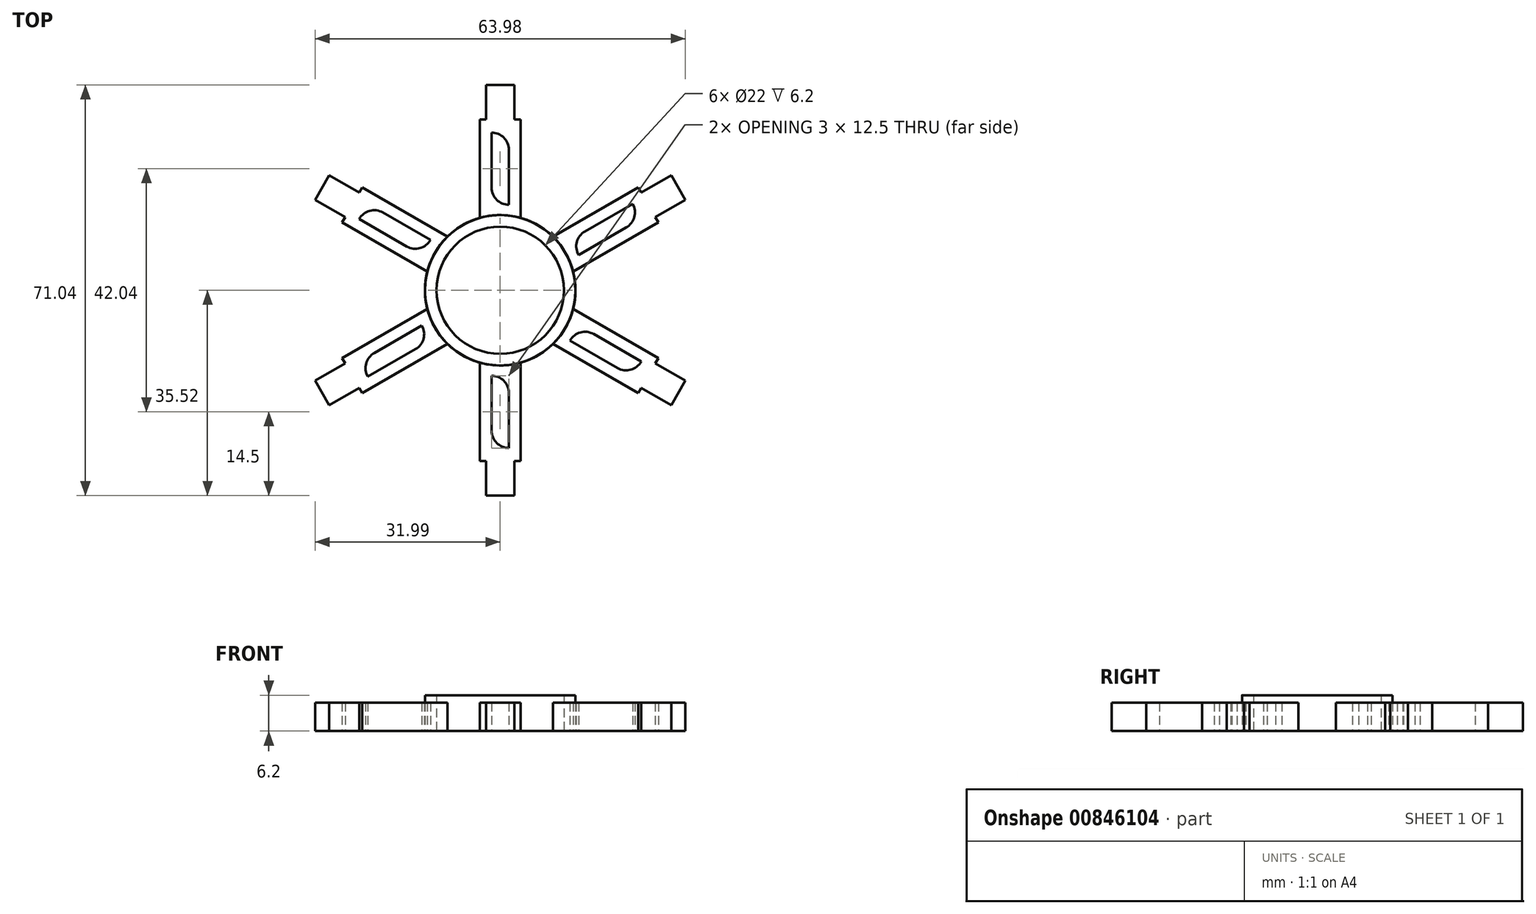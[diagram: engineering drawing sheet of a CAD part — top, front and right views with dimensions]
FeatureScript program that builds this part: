
annotation { "Feature Type Name" : "Feature", "Feature Type Description" : "" }
export const myFeature = defineFeature(function(context is Context, id is Id, definition is map)
    precondition{}
    {
        {
            var Q0;
            Q0=qCreatedBy(makeId("Top.planeOp"),FACE);
            var sketch = newSketch(context, id + "F0", { "sketchPlane" : qUnion([Q0])});
            skCircle(sketch, "E0", {"center": v(0, 0) * mm, "radius": 11 * mm});
            skLineSegment(sketch, "E1", {"start": v(0, 0) * mm, "end": v(11, 0) * mm});
            skCircle(sketch, "E2", {"center": v(0, 0) * mm, "radius": 13 * mm});
            skLineSegment(sketch, "E3", {"start": v(0, 0) * mm, "end": v(0, -13) * mm});
            skLineSegment(sketch, "E4.top", {"start": v(3.5, 29.52) * mm, "end": v(-3.5, 29.52) * mm});
            skLineSegment(sketch, "E4.left", {"start": v(3.5, 12.52) * mm, "end": v(3.5, 29.52) * mm});
            skLineSegment(sketch, "E4.right", {"start": v(-3.5, 12.52) * mm, "end": v(-3.5, 29.52) * mm});
            skPoint(sketch, "E4.middle", {"position": v(0, 21.02) * mm});
            skLineSegment(sketch, "E5.bottom", {"start": v(2.45, 29.52) * mm, "end": v(-2.45, 29.52) * mm});
            skLineSegment(sketch, "E5.top", {"start": v(2.45, 35.52) * mm, "end": v(-2.45, 35.52) * mm});
            skLineSegment(sketch, "E5.left", {"start": v(2.45, 29.52) * mm, "end": v(2.45, 35.52) * mm});
            skLineSegment(sketch, "E5.right", {"start": v(-2.45, 29.52) * mm, "end": v(-2.45, 35.52) * mm});
            skPoint(sketch, "E5.middle", {"position": v(0, 32.52) * mm});
            skLineSegment(sketch, "E6.bottom", {"start": v(1.5, 14.77) * mm, "end": v(1.5, 14.77) * mm});
            skLineSegment(sketch, "E6.top", {"start": v(-1.5, 27.27) * mm, "end": v(-1.5, 27.27) * mm});
            skLineSegment(sketch, "E6.left", {"start": v(1.5, 14.77) * mm, "end": v(1.5, 24.27) * mm});
            skLineSegment(sketch, "E6.right", {"start": v(-1.5, 17.77) * mm, "end": v(-1.5, 27.27) * mm});
            skPoint(sketch, "E7.visualSharp", {"position": v(-1.5, 14.77) * mm});
            skArc(sketch, "E7.filletArc", {"start": v(-1.5, 17.77) * mm, "mid": v(-0.62, 15.65) * mm, "end": v(1.5, 14.77) * mm});
            skPoint(sketch, "E8.visualSharp", {"position": v(1.5, 27.27) * mm});
            skArc(sketch, "E8.filletArc", {"start": v(1.5, 24.27) * mm, "mid": v(0.62, 26.4) * mm, "end": v(-1.5, 27.27) * mm});
            skSolve(sketch);
        }
        {
            var Q0;
            {var subQ0=sQuery(id+"F0.wireOp",EDGE,"E2");var subQ1=makeQuery(id+"F0.imprint","IMPRINT",VERTEX,{"derivedFrom":subQ0});Q0=makeQuery(id+"F0.imprint","IMPRINT",FACE,{"disambiguationData":[TD([[makeQuery(id+"F0.imprint","IMPRINT",EDGE,{"disambiguationData":[TD([[subQ1,1.0]])],"derivedFrom":subQ0}),1.0]])]});}
            extrude(context, id + "F1", {"entities" : qUnion([Q0]), "depth" : 6.2 * mm, "offsetDistance" : 25.4 * mm});
        }
        {
            var Q0;
            {var subQ1=sQuery(id+"F0.wireOp",EDGE,"E4.left");Q0=makeQuery(id+"F0.imprint","IMPRINT",FACE,{"disambiguationData":[TD([[makeQuery(id+"F0.imprint","IMPRINT",EDGE,{"derivedFrom":subQ1}),1.0]])]});}
            var Q1;
            Q1=makeQuery(id+"F0.imprint","IMPRINT",FACE,{"disambiguationData":[TD([[makeQuery(id+"F0.imprint","IMPRINT",EDGE,{"derivedFrom":sQuery(id+"F0.wireOp",EDGE,"E5.top")}),1.0]])]});
            extrude(context, id + "F2", {"entities" : qUnion([Q0, Q1]), "operationType" : NewBodyOperationType.ADD, "depth" : 4.9 * mm, "offsetDistance" : 25.4 * mm});
        }
        {
            var Q0;
            Q0=makeQuery(id+"F1.opExtrude","SWEPT_BODY",BODY,{"disambiguationData":[OSD([sQuery(id+"F0.wireOp",EDGE,"E0"),sQuery(id+"F0.wireOp",EDGE,"E2")])]});
            var Q1;
            Q1=makeQuery(id+"F1.opExtrude","CAP_EDGE",EDGE,{"disambiguationData":[OSD([sQuery(id+"F0.wireOp",EDGE,"E0")])],"isStart":false});
            circularPattern(context, id + "F3", {"entities" : qUnion([Q0]), "axis" : qUnion([Q1]), "angle" : 360 * degree, "instanceCount" : 6, "equalSpace" : true});
        }
    });
